# Revit family: Detector óptico para conductos_Aguilera Electronica
name_source: partatom
category: Dispositivos de alarma de incendios
revit_build: Autodesk Revit 2017 (Build: 20160225_1515(x64)
units: mm (PartAtom-declared; Revit-internal decimal feet)

## family parameters
Anfitrión = Cara
Compartido = No
Corte con vacíos al cargar = No
Cota de conector redondo = Diámetro de uso
Mantener orientación de anotación = Sí
Número OmniClass = 23.85.30.21.11.11.11
Punto de cálculo de habitación = No
Tipo de pieza = Normal
Título OmniClass = Smoke Detectors

## types (1)
- Detector óptico para conductos
    Altura = 135 mm  [stored 0.442913 ft]
    Anchura = 85 mm  [stored 0.278871 ft]
    Descripción = Equipo fabricado por Aguilera Electrónica, formado por un detector óptico algorítmico AE/SA-OPI y caja metálica provista con piloto de alarma, racor para entrada de cables y racores para tubos sondas que toman las muestras del interior de los conductos.
    Elevación por defecto = 1200 mm
    Fabricante = Aguilera Electrónica
    Longitud = 160 mm  [stored 0.524934 ft]
    Modelo = AE/SA-OPIC
    Simbolo = Sí
    Símbolo texto modelo = Sí
    URL = https://aguilera.es

note: [stored X ft] marks values corroborated as IEEE doubles in the binary element streams (Revit-internal decimal feet)
